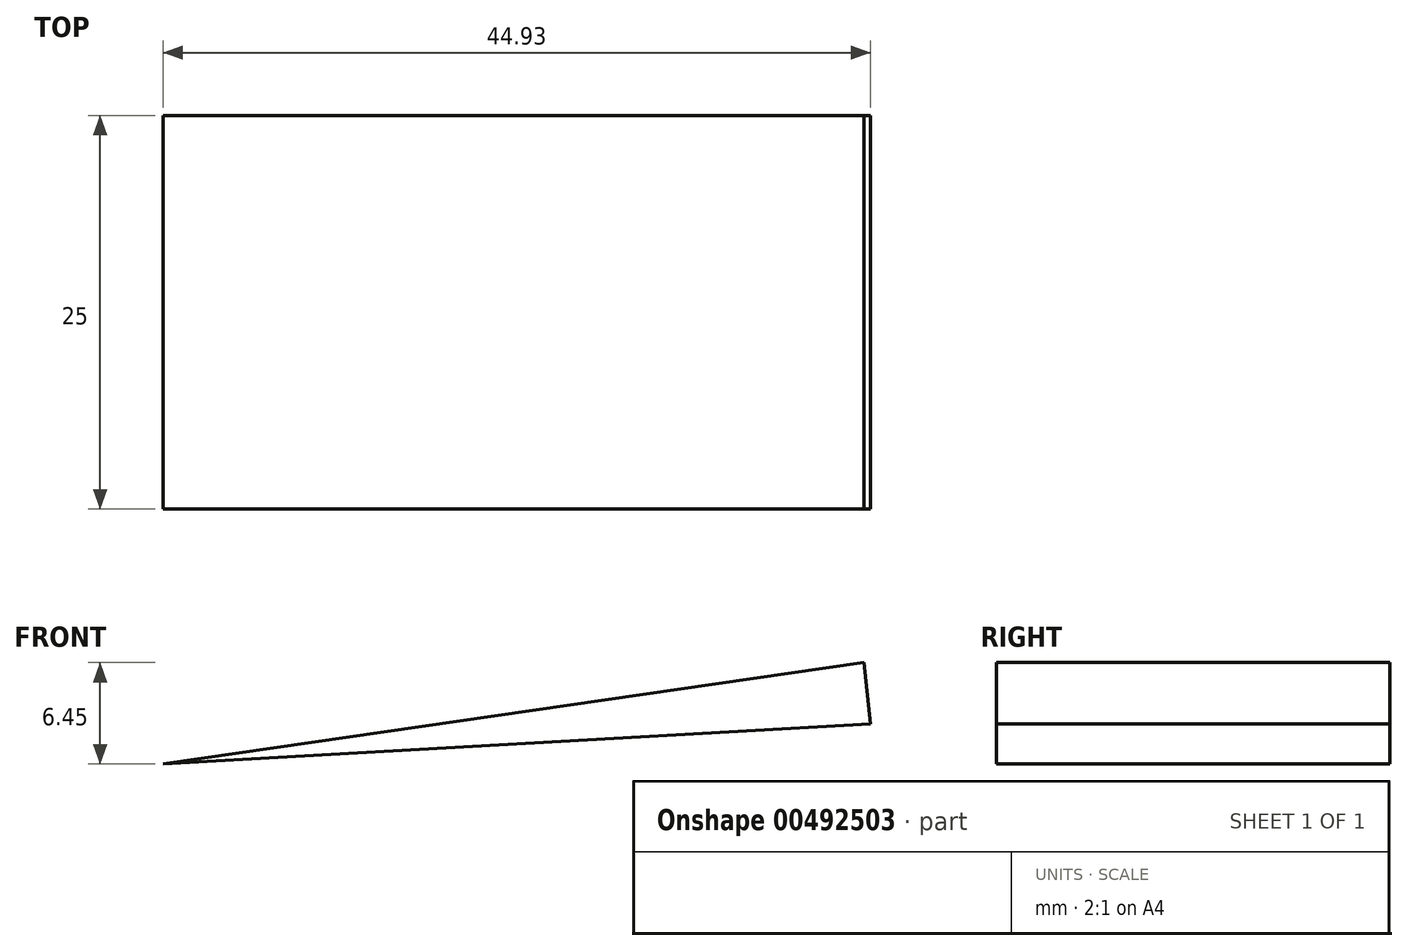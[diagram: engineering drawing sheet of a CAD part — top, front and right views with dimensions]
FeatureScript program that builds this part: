
annotation { "Feature Type Name" : "Feature", "Feature Type Description" : "" }
export const myFeature = defineFeature(function(context is Context, id is Id, definition is map)
    precondition{}
    {
        {
            var Q0;
            Q0=qCreatedBy(makeId("Front.planeOp"),FACE);
            var sketch = newSketch(context, id + "F0", { "sketchPlane" : qUnion([Q0])});
            skLineSegment(sketch, "E0", {"start": v(-20.02, 0) * mm, "end": v(24.52, 6.45) * mm});
            skLineSegment(sketch, "E1", {"start": v(-20.02, 0) * mm, "end": v(24.9, 2.55) * mm});
            skLineSegment(sketch, "E2", {"start": v(24.52, 6.45) * mm, "end": v(24.9, 2.55) * mm});
            skSolve(sketch);
        }
        {
            var Q0;
            Q0=makeQuery(id+"F0.imprint","IMPRINT",FACE,{"disambiguationData":[TD([[makeQuery(id+"F0.imprint","IMPRINT",EDGE,{"derivedFrom":sQuery(id+"F0.wireOp",EDGE,"E0")}),-1.0]])]});
            extrude(context, id + "F1", {"entities" : qUnion([Q0]), "endBound" : BoundingType.SYMMETRIC, "depth" : 25 * mm});
        }
    });
